# Revit family: Shinhoo_MEGA_S
name_source: partatom
category: Оборудование
units: mm (PartAtom-declared; Revit-internal decimal feet)

## family parameters
Всегда вертикально = Нет
Классификация = Нет
На основе рабочей плоскости = Нет
Общий = Нет
При загрузке вырезать с полостями = Нет
Размер круглого соединителя = Использовать диаметр
Тип детали = Вставляется
Точка расчета площади = Нет

## types (2) — shared parameters
ADSK_URL страницы изделия = https://shinhoopump.ru
ADSK_Версия Revit = 2019
ADSK_Версия семейства = 1.0
ADSK_Единица измерения = шт
ADSK_Завод-изготовитель = Shinhoo
ADSK_Количество = 1
ADSK_Коэффициент мощности = 1
ADSK_Материал = Чугун с катафорезным покрытием
ADSK_Напряжение = 230 В
ADSK_Номинальная мощность = 750 Вт
ADSK_Обозначение = ГОСТ 31839-2012, ГОСТ 12.2.007.0-75, ГОСТ 12.2.003-91, ГОСТ Р МЭК 60204-1-2007,  ГОСТ 30804
ADSK_Полная мощность = 750 В·А
ADSK_Ток = 3 А
H = 380 мм
H2 = 307 мм
URL = https://shinhoopump.ru
r6 = 55 мм
Изготовитель = Shinhoo
Класс защиты (IP) = IPX4D
Разработчик = ООО ПРОРУБИМ
Разработчик (телефон) = +7(495)649-85-43
Скорость вращения = 2850
Степень защиты от удара (IK) = IK04
Тип Насоса = Регулируемый высокоэффективный циркуляционный насос с «мокрым» ротором
Тип основания = встроенный

## per-type parameters (varying)
| type | ADSK_Код изделия | ADSK_Масса | ADSK_Масса_Текст | ADSK_Наименование | ADSK_Наименование краткое | ADSK_Расход жидкости | B | B1 | B2 | D1 | DN | H1 | L | b1_20 | d1 | d1_r1 | d2 | d6 | r1 | r1_1 | r1_3 | Группа модели |
| MEGA S 50-18F 280 1x230В - 71121007 | 71121007 | 22 | 22 | Регулируемый высокоэффективный циркуляционный насос с «мокрым» ротором MEGA S 50-18F 280 1x230В | MEGA S 50-18F 280 1x230В | 0.009028 м³/с | 290 мм | 145 мм | 145 мм | 165 мм | 50 мм | 73 мм | 280 мм | 124 мм | 25 мм | 75 мм | 120 мм | 50 мм | 13 мм | 14 мм | 19 мм | MEGA S 50-18F 280 1x230В |
| MEGA S 65-12F 340 1x230В - 71121008 | 71121008 | 24 | 24 | Регулируемый высокоэффективный циркуляционный насос с «мокрым» ротором MEGA S 65-12F 340 1x230В | MEGA S 65-12F 340 1x230В | 0.009722 м³/с | 266 мм | 133 мм | 133 мм | 185 мм | 65 мм | 74 мм | 342 мм | 114 мм | 33 мм | 98 мм | 165 мм | 65 мм | 16 мм | 17 мм | 24 мм | MEGA S 65-12F 340 1x230В |

## geometry (parser evidence)
native form markers: Sweep x2
no freeform markers — native parametric forms only
